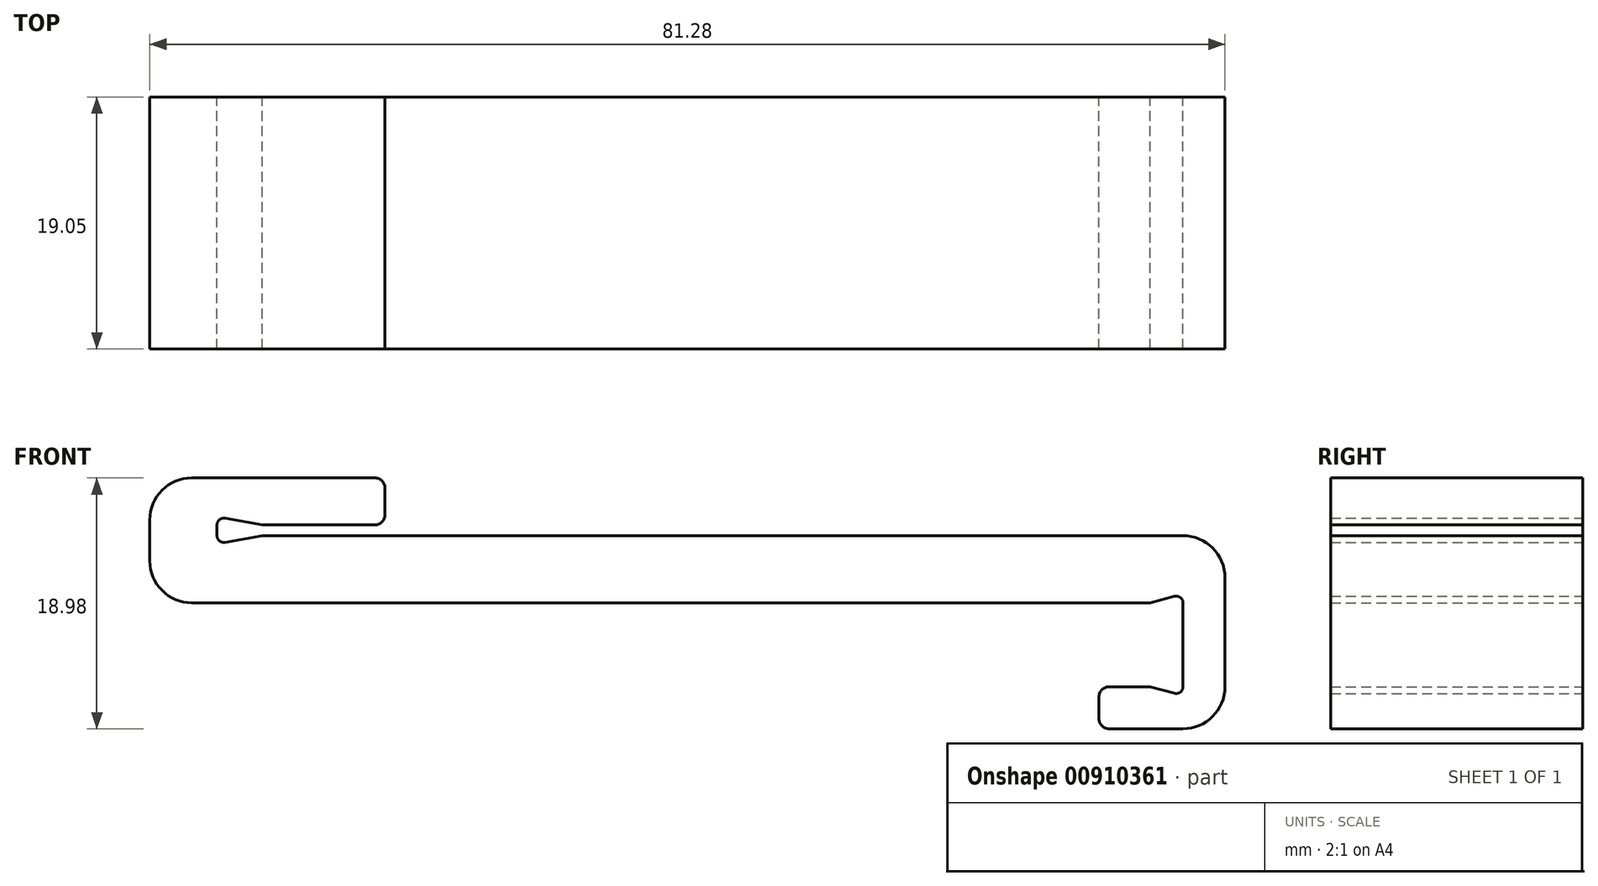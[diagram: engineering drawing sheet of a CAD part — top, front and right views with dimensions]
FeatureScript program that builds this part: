
annotation { "Feature Type Name" : "Feature", "Feature Type Description" : "" }
export const myFeature = defineFeature(function(context is Context, id is Id, definition is map)
    precondition{}
    {
        {
            var Q0;
            Q0=qCreatedBy(makeId("Front.planeOp"),FACE);
            var sketch = newSketch(context, id + "F0", { "sketchPlane" : qUnion([Q0])});
            skLineSegment(sketch, "E0", {"start": v(11.94, 0.81) * mm, "end": v(3.43, 0.81) * mm});
            skLineSegment(sketch, "E1", {"start": v(0, 0.81) * mm, "end": v(0, 0) * mm});
            skLineSegment(sketch, "E2", {"start": v(76.2, -3.17) * mm, "end": v(76.2, -11.43) * mm});
            skLineSegment(sketch, "E3", {"start": v(73.03, -14.6) * mm, "end": v(67.44, -14.6) * mm});
            skLineSegment(sketch, "E4", {"start": v(66.68, -13.84) * mm, "end": v(66.68, -12.2) * mm});
            skLineSegment(sketch, "E5", {"start": v(67.44, -11.43) * mm, "end": v(70.55, -11.43) * mm});
            skLineSegment(sketch, "E6", {"start": v(73.03, -11.43) * mm, "end": v(73.03, -5.08) * mm});
            skLineSegment(sketch, "E7", {"start": v(-5.08, -1.9) * mm, "end": v(-5.08, 1.2) * mm});
            skLineSegment(sketch, "E8", {"start": v(-1.9, 4.37) * mm, "end": v(11.94, 4.37) * mm});
            skLineSegment(sketch, "E9", {"start": v(12.7, 3.6) * mm, "end": v(12.7, 1.57) * mm});
            skArc(sketch, "E10", {"start": v(0.6, 1.31) * mm, "mid": v(0.18, 1.2) * mm, "end": v(0, 0.81) * mm});
            skArc(sketch, "E11", {"start": v(0, 0) * mm, "mid": v(0.18, -0.39) * mm, "end": v(0.6, -0.5) * mm});
            skLineSegment(sketch, "E12", {"start": v(0.6, -0.5) * mm, "end": v(3.43, 0) * mm});
            skLineSegment(sketch, "E13", {"start": v(0.6, 1.31) * mm, "end": v(3.43, 0.81) * mm});
            skLineSegment(sketch, "E14.trimOffspring", {"start": v(3.43, 0) * mm, "end": v(73.03, 0) * mm});
            skPoint(sketch, "E15.visualSharp", {"position": v(12.7, 0.81) * mm});
            skArc(sketch, "E15.filletArc", {"start": v(11.94, 0.81) * mm, "mid": v(12.48, 1.04) * mm, "end": v(12.7, 1.57) * mm});
            skPoint(sketch, "E16.visualSharp", {"position": v(12.7, 4.37) * mm});
            skArc(sketch, "E16.filletArc", {"start": v(12.7, 3.6) * mm, "mid": v(12.48, 4.15) * mm, "end": v(11.94, 4.37) * mm});
            skPoint(sketch, "E17.visualSharp", {"position": v(66.68, -11.43) * mm});
            skArc(sketch, "E17.filletArc", {"start": v(67.44, -11.43) * mm, "mid": v(66.9, -11.65) * mm, "end": v(66.68, -12.2) * mm});
            skPoint(sketch, "E18.visualSharp", {"position": v(66.68, -14.6) * mm});
            skArc(sketch, "E18.filletArc", {"start": v(66.68, -13.84) * mm, "mid": v(66.9, -14.38) * mm, "end": v(67.44, -14.6) * mm});
            skPoint(sketch, "E19.visualSharp", {"position": v(-5.08, 4.37) * mm});
            skArc(sketch, "E19.filletArc", {"start": v(-1.9, 4.37) * mm, "mid": v(-4.15, 3.44) * mm, "end": v(-5.08, 1.2) * mm});
            skPoint(sketch, "E20.visualSharp", {"position": v(-5.08, -5.08) * mm});
            skArc(sketch, "E20.filletArc", {"start": v(-5.08, -1.9) * mm, "mid": v(-4.15, -4.15) * mm, "end": v(-1.9, -5.08) * mm});
            skPoint(sketch, "E21.visualSharp", {"position": v(76.2, 0) * mm});
            skArc(sketch, "E21.filletArc", {"start": v(76.2, -3.17) * mm, "mid": v(75.27, -0.93) * mm, "end": v(73.03, 0) * mm});
            skPoint(sketch, "E22.visualSharp", {"position": v(76.2, -14.6) * mm});
            skArc(sketch, "E22.filletArc", {"start": v(73.03, -14.6) * mm, "mid": v(75.27, -13.68) * mm, "end": v(76.2, -11.43) * mm});
            skArc(sketch, "E23", {"start": v(73.03, -5.08) * mm, "mid": v(72.83, -4.68) * mm, "end": v(72.39, -4.59) * mm});
            skLineSegment(sketch, "E24", {"start": v(72.39, -4.59) * mm, "end": v(70.55, -5.08) * mm});
            skArc(sketch, "E25", {"start": v(72.39, -11.92) * mm, "mid": v(72.83, -11.83) * mm, "end": v(73.02, -11.43) * mm});
            skLineSegment(sketch, "E26", {"start": v(72.39, -11.92) * mm, "end": v(70.55, -11.43) * mm});
            skLineSegment(sketch, "E27.trimOffspring", {"start": v(70.55, -5.08) * mm, "end": v(-1.9, -5.08) * mm});
            skSolve(sketch);
        }
        {
            var Q0;
            Q0=qSketchRegion(id+"F0",true);
            extrude(context, id + "F1", {"entities" : qUnion([Q0]), "depth" : 19.05 * mm, "offsetDistance" : 25.4 * mm});
        }
    });
